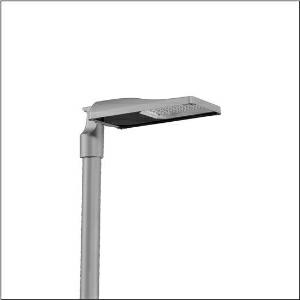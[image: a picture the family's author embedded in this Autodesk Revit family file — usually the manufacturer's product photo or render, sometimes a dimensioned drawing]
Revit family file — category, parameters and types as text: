
# Revit family: streetlight_sl_31_mini___st1_0a_5xh2d31b08ha_780c
name_source: partatom
category: Lighting Fixtures
units: mm (PartAtom-declared; Revit-internal decimal feet)

## family parameters
Cut with Voids When Loaded = No
Host = Face
Light Source = No
Part Type = Normal
Room Calculation Point = No
Round Connector Dimension = Use Diameter
Shared = No

## types (1)
- --- (1 x LED, 9240 lm, 68.3 W, 3000K)
    Apparent Load = 68 VA
    CIE Flux Codes = 37 72 97 100 100
    Color Rendering = 70
    Color Temperature = 3000K
    Default Elevation = 1800 mm
    Description = Streetlight SL 31 mini Easy, LST, Desk-Remote mast luminaire for post-top, side-entry; light control with lens of PMMA; light distribution: ST1.0a, direct asymmetric distribution, for standard-compliant lighting for roads and squares; LED: luminous flux: 9.240lm, light colour: 730, colour temperature: 3000K; luminous efficacy: 135,3lm/W; control: pre-setting: linear dimming characteristic, flexible luminous flux parameterisation, time-dependent luminous flux control, constant luminous flux control, power reduction, intelligent temperature release in ECG and LED module, overheat protection; luminaire housing, of diecast aluminium, SITECO metallic grey (DB 702S), corrosivity category C5 high according to DIN EN ISO 12944; cover of toughened safety glass, transparent, mast flange of diecast aluminium, SITECO metallic grey (DB 702S), spigot size: 76/60mm, mast flange included unmounted; with cable H07RN-F 5x 1.5mm², cable length: 8,5m, connection cable pre-assembled; mains connection: 220..240V, AC, 50/60Hz; power consumption (at start of service life): 68,3W / (at end of service life): 74,8W / (with reduced operation 50%): 29,7W; protection rating (complete): IP66; insulation class (complete): insulation class II (safety insulation); impact resistance: IK10; certification: CE, ENEC, ENEC+, VDE, UKCA; permissible operating ambient temperature for outdoor applications: -40..+50°C; packaging unit: 1 piece

Light Distribution: ST1.0a
    Height = 76 mm
    Lamp = 1 x LED
    Lamp Light Flux = 9240 lm
    Lamp Power = 68.3 W
    Lamp count = 1
    Length = 547 mm
    Luminous efficacy = 135 lm/W
    Manufacturer = Siteco
    ModVariant = No
    Model = 5XH2D31B08HA
    Number of Poles = 1
    OnlyDefault = Yes
    Power Factor = 1
    Product Name = Streetlight SL 31 mini | ST1.0a
    Product group = mast luminaire | pylon top
    ProductGroupID = 6100
    Protection Class = Protection class II
    Protection Degree = IP 66
    RLX_Detail_Level = 1
    RLX_Emergency_Light_Flux = 0 lm
    RLX_Emergency_Type = 0
    RLX_Emergency_Type_DB = No
    RlxData = <blob elided: 39453 chars, md5=7b5b0bfe>
    Socket = socket
    Standby Power = 0 W
    System Light Flux = 9240 lm
    System Power = 68 W
    Type Comments = factory setting: luminous flux: 100 % | dim-lin: 254 | 693 mA
    Type Image = l_1300326.jpg
    URL = http://relux.com
    VarID = @adj_061651
    Voltage = 0 V
    Weight = 0.00 kg
    Width = 265 mm

## geometry (parser evidence)
native form markers: Blend x4, Sweep x11
no freeform markers — native parametric forms only
